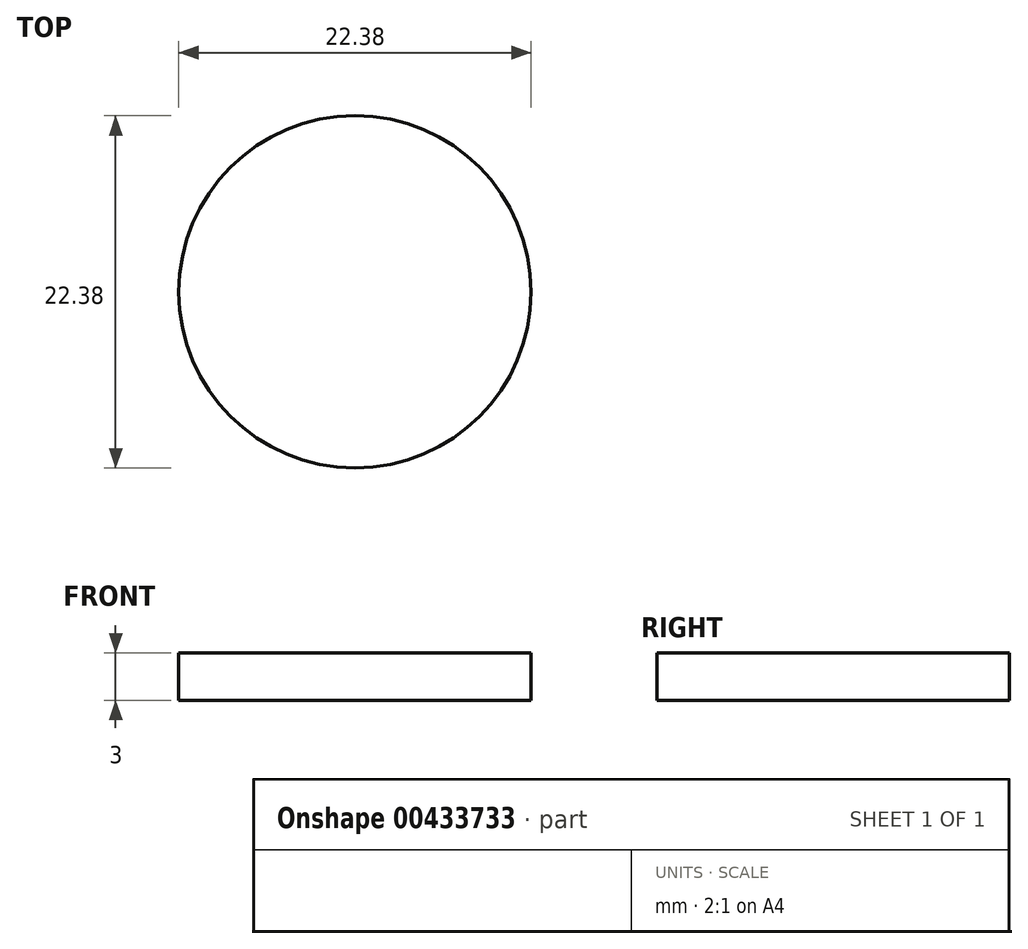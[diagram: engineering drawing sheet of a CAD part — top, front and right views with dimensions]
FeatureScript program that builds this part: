
annotation { "Feature Type Name" : "Feature", "Feature Type Description" : "" }
export const myFeature = defineFeature(function(context is Context, id is Id, definition is map)
    precondition{}
    {
        {
            var Q0;
            Q0=qCreatedBy(makeId("Top.planeOp"),FACE);
            var sketch = newSketch(context, id + "F0", { "sketchPlane" : qUnion([Q0])});
            skCircle(sketch, "E0", {"center": v(-52.95, 28.17) * mm, "radius": 11.19 * mm});
            skSolve(sketch);
        }
        {
            var Q0;
            Q0=makeQuery(id+"F0.imprint","IMPRINT",FACE,{"disambiguationData":[TD([[makeQuery(id+"F0.imprint","IMPRINT",EDGE,{"derivedFrom":sQuery(id+"F0.wireOp",EDGE,"E0")}),1.0]])]});
            extrude(context, id + "F1", {"entities" : qUnion([Q0]), "depth" : 3 * mm});
        }
    });
